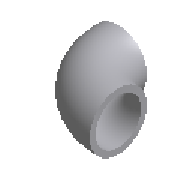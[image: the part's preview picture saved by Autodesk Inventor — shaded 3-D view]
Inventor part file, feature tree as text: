
AUTODESK INVENTOR PART (.ipt)
format: ipt  version: 2024.2 (Build 282272000, 272)  size: 192,512 bytes
history: native  units: mm (DEFAULTED — no unit token found)
features: other x4, sweep x1
ambient origin geometry x8: Origin, YZ Plane, XZ Plane, XY Plane, X Axis, Y Axis, Z Axis, Center Point
bodies: Solid1 (feature_tree)
feature tree (5):
  sweep  "Sweep1"
  other  "Work Point1"
  other  "Work Axis1"
  other  "Work Point2"
  other  "Work Axis2"
